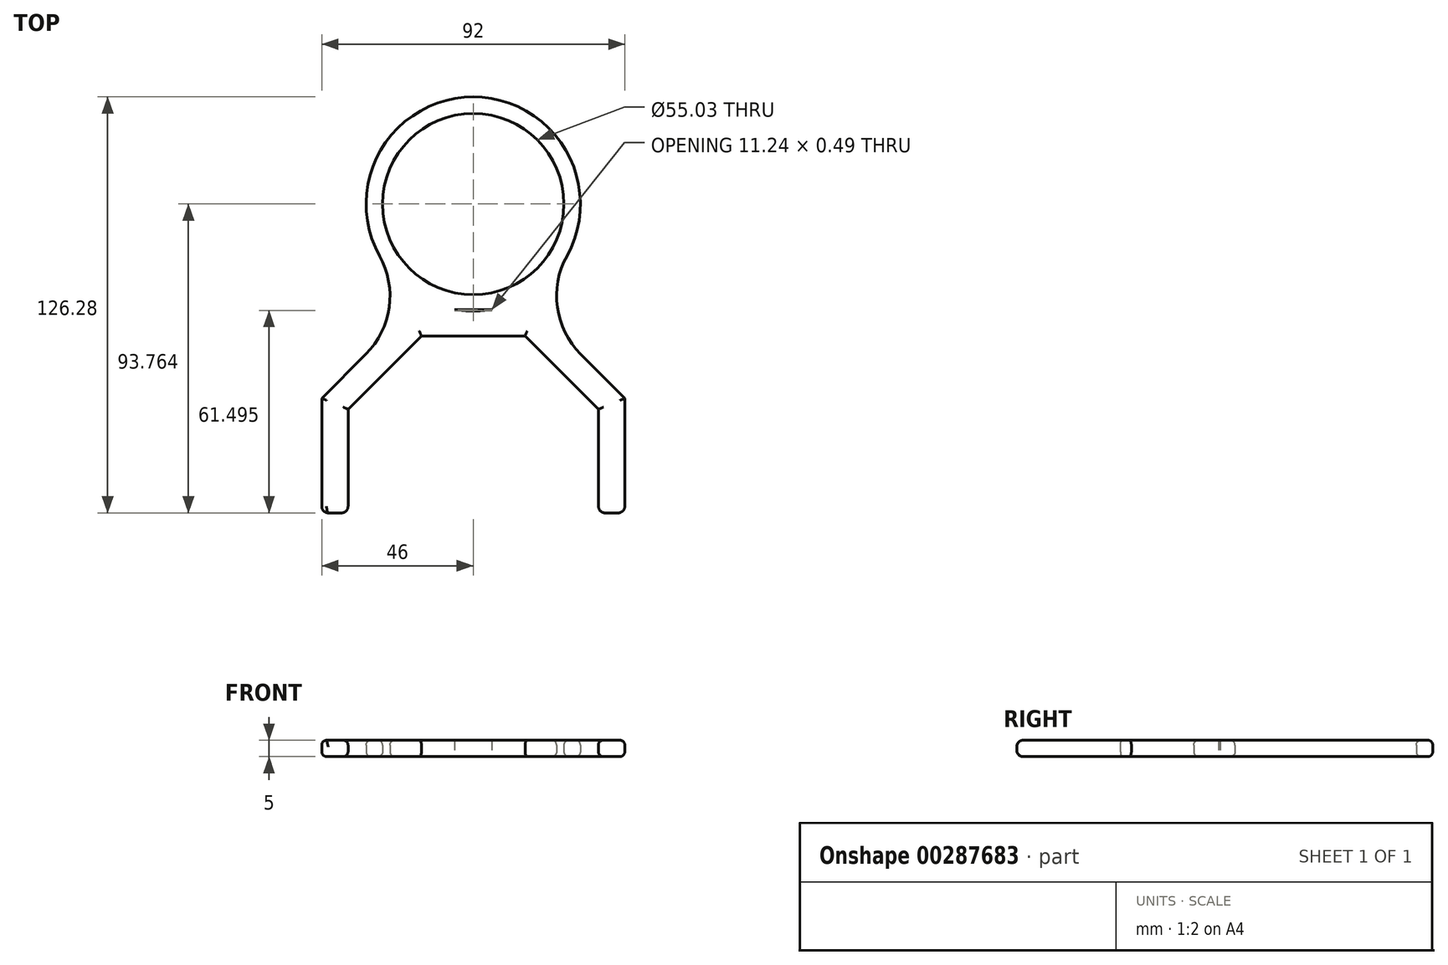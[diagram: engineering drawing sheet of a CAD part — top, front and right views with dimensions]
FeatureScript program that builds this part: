
annotation { "Feature Type Name" : "Feature", "Feature Type Description" : "" }
export const myFeature = defineFeature(function(context is Context, id is Id, definition is map)
    precondition{}
    {
        {
            var Q0;
            Q0=qCreatedBy(makeId("Top.planeOp"),FACE);
            var sketch = newSketch(context, id + "F0", { "sketchPlane" : qUnion([Q0])});
            skLineSegment(sketch, "E0.top", {"start": v(-46.8, 110.54) * mm, "end": v(46.8, 110.54) * mm});
            skLineSegment(sketch, "E0.left", {"start": v(-46.8, -31.71) * mm, "end": v(-46.8, 110.54) * mm});
            skLineSegment(sketch, "E0.right", {"start": v(46.8, -30.95) * mm, "end": v(46.8, 110.54) * mm});
            skCircle(sketch, "E1", {"center": v(0, 78.02) * mm, "radius": 32.51 * mm});
            skPoint(sketch, "E1.centerSnap0", {"position": v(0, 110.54) * mm});
            skLineSegment(sketch, "E2", {"start": v(-19.05, 46) * mm, "end": v(-28.16, 61.77) * mm});
            skLineSegment(sketch, "E3", {"start": v(28.16, 61.77) * mm, "end": v(19.05, 46) * mm});
            skCircle(sketch, "E4.0", {"center": v(0, 78.02) * mm, "radius": 27.51 * mm});
            skCircle(sketch, "E5.cCircle", {"center": v(0, 0) * mm, "radius": 38 * mm, "construction": true});
            skLineSegment(sketch, "E5.0", {"start": v(15.74, 38) * mm, "end": v(38, 15.74) * mm});
            skLineSegment(sketch, "E5.1", {"start": v(38, 15.74) * mm, "end": v(38, -15.74) * mm});
            skLineSegment(sketch, "E5.2", {"start": v(38, -15.74) * mm, "end": v(15.74, -38) * mm});
            skLineSegment(sketch, "E5.3", {"start": v(15.74, -38) * mm, "end": v(-15.74, -38) * mm});
            skLineSegment(sketch, "E5.4", {"start": v(-15.74, -38) * mm, "end": v(-38, -15.74) * mm});
            skLineSegment(sketch, "E5.5", {"start": v(-38, -15.74) * mm, "end": v(-38, 15.74) * mm});
            skLineSegment(sketch, "E5.6", {"start": v(-38, 15.74) * mm, "end": v(-15.74, 38) * mm});
            skLineSegment(sketch, "E5.7", {"start": v(-15.74, 38) * mm, "end": v(15.74, 38) * mm});
            skPoint(sketch, "E5.0.midPoint", {"position": v(26.87, 26.87) * mm});
            skLineSegment(sketch, "E6.0", {"start": v(-19.05, 46) * mm, "end": v(19.05, 46) * mm});
            skLineSegment(sketch, "E6.1", {"start": v(-46, 19.05) * mm, "end": v(-19.05, 46) * mm});
            skLineSegment(sketch, "E6.2", {"start": v(19.05, 46) * mm, "end": v(46, 19.05) * mm});
            skLineSegment(sketch, "E6.3", {"start": v(-46, -19.05) * mm, "end": v(-46, 19.05) * mm});
            skLineSegment(sketch, "E6.4", {"start": v(46, 19.05) * mm, "end": v(46, -19.05) * mm});
            skLineSegment(sketch, "E6.5", {"start": v(46, -19.05) * mm, "end": v(19.05, -46) * mm});
            skLineSegment(sketch, "E6.6", {"start": v(19.05, -46) * mm, "end": v(-19.05, -46) * mm});
            skLineSegment(sketch, "E6.7", {"start": v(-19.05, -46) * mm, "end": v(-46, -19.05) * mm});
            skLineSegment(sketch, "E7", {"start": v(-46.8, -15.74) * mm, "end": v(46.8, -15.74) * mm});
            skSolve(sketch);
        }
        {
            var Q0;
            Q0=makeQuery(id+"F0.imprint","IMPRINT",FACE,{"disambiguationData":[TD([[makeQuery(id+"F0.imprint","IMPRINT",EDGE,{"derivedFrom":sQuery(id+"F0.wireOp",EDGE,"E4.0")}),-1.0]])]});
            var Q1;
            {var subQ0=sQuery(id+"F0.wireOp",EDGE,"E2");Q1=makeQuery(id+"F0.imprint","IMPRINT",FACE,{"disambiguationData":[TD([[makeQuery(id+"F0.imprint","IMPRINT",EDGE,{"derivedFrom":subQ0}),-1.0]])]});}
            var Q2;
            Q2=makeQuery(id+"F0.imprint","IMPRINT",FACE,{"disambiguationData":[TD([[makeQuery(id+"F0.imprint","IMPRINT",EDGE,{"derivedFrom":sQuery(id+"F0.wireOp",EDGE,"1d4a6ea0-dfed-4e67-ae61-2447e46420ab.0")}),1.0]])]});
            var Q3;
            Q3=makeQuery(id+"F0.imprint","IMPRINT",FACE,{"disambiguationData":[TD([[makeQuery(id+"F0.imprint","IMPRINT",EDGE,{"derivedFrom":sQuery(id+"F0.wireOp",EDGE,"E5.0")}),1.0]])]});
            var Q4;
            {var subQ0=sQuery(id+"F0.wireOp",EDGE,"E3");Q4=makeQuery(id+"F0.imprint","IMPRINT",FACE,{"disambiguationData":[TD([[makeQuery(id+"F0.imprint","IMPRINT",EDGE,{"derivedFrom":subQ0}),-1.0]])]});}
            var Q5;
            {var subQ0=sQuery(id+"F0.wireOp",EDGE,"E6.0");var subQ1=sQuery(id+"F0.wireOp",EDGE,"E1");var subQ2=makeQuery(id+"F0.imprint","INTERSECT",VERTEX,{"disambiguationData":[OD(0.0)],"derivedFrom":[subQ1,subQ0]});Q5=makeQuery(id+"F0.imprint","IMPRINT",FACE,{"disambiguationData":[TD([[makeQuery(id+"F0.imprint","IMPRINT",EDGE,{"disambiguationData":[TD([[subQ2,-1.0]])],"derivedFrom":subQ1}),1.0]])]});}
            extrude(context, id + "F1", {"entities" : qUnion([Q0, Q1, Q2, Q3, Q4, Q5]), "depth" : 5 * mm});
        }
        {
            var Q0;
            Q0=makeQuery(id+"F1.opExtrude","SWEPT_EDGE",EDGE,{"disambiguationData":[OSD([sQuery(id+"F0.wireOp",EDGE,"E3"),sQuery(id+"F0.wireOp",EDGE,"E6.0"),sQuery(id+"F0.wireOp",EDGE,"E6.2")])]});
            var Q1;
            Q1=makeQuery(id+"F1.opExtrude","SWEPT_EDGE",EDGE,{"disambiguationData":[OSD([sQuery(id+"F0.wireOp",EDGE,"E2"),sQuery(id+"F0.wireOp",EDGE,"E6.0"),sQuery(id+"F0.wireOp",EDGE,"E6.1")])]});
            fillet(context, id + "F2", {"entities" : qUnion([Q0, Q1]), "radius" : 25 * mm, "tangentPropagation" : true, "allowEdgeOverflow" : false});
        }
        {
            var Q0;
            Q0=makeQuery(id+"F1.opExtrude","CAP_EDGE",EDGE,{"disambiguationData":[OSD([sQuery(id+"F0.wireOp",EDGE,"E4.0")])],"isStart":false});
            var Q1;
            Q1=makeQuery(id+"F1.opExtrude","CAP_EDGE",EDGE,{"disambiguationData":[OSD([sQuery(id+"F0.wireOp",EDGE,"E2")])],"isStart":false});
            var Q2;
            {var subQ0=sQuery(id+"F0.wireOp",EDGE,"E2");var subQ1=sQuery(id+"F0.wireOp",EDGE,"d9d4c305-0230-4e48-996b-9e131303d5f2.3");Q2=makeQuery(id+"F2.opFillet","BLEND_EDGE",EDGE,{"blendedFrom":[makeQuery(id+"F1.opExtrude","SWEPT_EDGE",EDGE,{"disambiguationData":[OSD([subQ1,subQ0])]}),makeQuery(id+"F1.opExtrude","CAP_FACE",FACE,{"disambiguationData":[OSD([sQuery(id+"F0.wireOp",EDGE,"1d4a6ea0-dfed-4e67-ae61-2447e46420ab.0"),sQuery(id+"F0.wireOp",EDGE,"1d4a6ea0-dfed-4e67-ae61-2447e46420ab.1"),sQuery(id+"F0.wireOp",EDGE,"1d4a6ea0-dfed-4e67-ae61-2447e46420ab.4"),sQuery(id+"F0.wireOp",EDGE,"1d4a6ea0-dfed-4e67-ae61-2447e46420ab.5"),sQuery(id+"F0.wireOp",EDGE,"d9d4c305-0230-4e48-996b-9e131303d5f2.1"),subQ1,sQuery(id+"F0.wireOp",EDGE,"E0.bottom"),sQuery(id+"F0.wireOp",EDGE,"E0.left"),sQuery(id+"F0.wireOp",EDGE,"E0.right"),sQuery(id+"F0.wireOp",EDGE,"E1"),subQ0,sQuery(id+"F0.wireOp",EDGE,"E3"),sQuery(id+"F0.wireOp",EDGE,"E4.0")])],"isStart":true})],"blendedInto":[makeQuery(id+"F1.opExtrude","CAP_FACE",FACE,{"disambiguationData":[OSD([sQuery(id+"F0.wireOp",EDGE,"1d4a6ea0-dfed-4e67-ae61-2447e46420ab.0"),sQuery(id+"F0.wireOp",EDGE,"1d4a6ea0-dfed-4e67-ae61-2447e46420ab.1"),sQuery(id+"F0.wireOp",EDGE,"1d4a6ea0-dfed-4e67-ae61-2447e46420ab.4"),sQuery(id+"F0.wireOp",EDGE,"1d4a6ea0-dfed-4e67-ae61-2447e46420ab.5"),sQuery(id+"F0.wireOp",EDGE,"d9d4c305-0230-4e48-996b-9e131303d5f2.1"),subQ1,sQuery(id+"F0.wireOp",EDGE,"E0.bottom"),sQuery(id+"F0.wireOp",EDGE,"E0.left"),sQuery(id+"F0.wireOp",EDGE,"E0.right"),sQuery(id+"F0.wireOp",EDGE,"E1"),subQ0,sQuery(id+"F0.wireOp",EDGE,"E3"),sQuery(id+"F0.wireOp",EDGE,"E4.0")])],"isStart":true})]});}
            var Q3;
            Q3=makeQuery(id+"F1.opExtrude","CAP_EDGE",EDGE,{"disambiguationData":[OSD([sQuery(id+"F0.wireOp",EDGE,"E4.0")])],"isStart":true});
            var Q4;
            Q4=makeQuery(id+"F1.opExtrude","CAP_EDGE",EDGE,{"disambiguationData":[OSD([sQuery(id+"F0.wireOp",EDGE,"1d4a6ea0-dfed-4e67-ae61-2447e46420ab.5")])],"isStart":false});
            var Q5;
            Q5=makeQuery(id+"F1.opExtrude","CAP_EDGE",EDGE,{"disambiguationData":[OSD([sQuery(id+"F0.wireOp",EDGE,"1d4a6ea0-dfed-4e67-ae61-2447e46420ab.0")])],"isStart":false});
            var Q6;
            Q6=makeQuery(id+"F1.opExtrude","CAP_EDGE",EDGE,{"disambiguationData":[OSD([sQuery(id+"F0.wireOp",EDGE,"1d4a6ea0-dfed-4e67-ae61-2447e46420ab.1")])],"isStart":false});
            var Q7;
            Q7=makeQuery(id+"F1.opExtrude","CAP_EDGE",EDGE,{"disambiguationData":[OSD([sQuery(id+"F0.wireOp",EDGE,"E0.right")])],"isStart":false});
            var Q8;
            Q8=makeQuery(id+"F1.opExtrude","CAP_EDGE",EDGE,{"disambiguationData":[OSD([sQuery(id+"F0.wireOp",EDGE,"1d4a6ea0-dfed-4e67-ae61-2447e46420ab.4")])],"isStart":false});
            var Q9;
            Q9=makeQuery(id+"F1.opExtrude","CAP_EDGE",EDGE,{"disambiguationData":[OSD([sQuery(id+"F0.wireOp",EDGE,"E0.left")])],"isStart":false});
            var Q10;
            Q10=makeQuery(id+"F1.opExtrude","CAP_EDGE",EDGE,{"disambiguationData":[OSD([sQuery(id+"F0.wireOp",EDGE,"E0.left")])],"isStart":true});
            var Q11;
            Q11=makeQuery(id+"F1.opExtrude","CAP_EDGE",EDGE,{"disambiguationData":[OSD([sQuery(id+"F0.wireOp",EDGE,"1d4a6ea0-dfed-4e67-ae61-2447e46420ab.5")])],"isStart":true});
            var Q12;
            Q12=makeQuery(id+"F1.opExtrude","CAP_EDGE",EDGE,{"disambiguationData":[OSD([sQuery(id+"F0.wireOp",EDGE,"1d4a6ea0-dfed-4e67-ae61-2447e46420ab.4")])],"isStart":true});
            var Q13;
            Q13=makeQuery(id+"F1.opExtrude","CAP_EDGE",EDGE,{"disambiguationData":[OSD([sQuery(id+"F0.wireOp",EDGE,"1d4a6ea0-dfed-4e67-ae61-2447e46420ab.1")])],"isStart":true});
            var Q14;
            Q14=makeQuery(id+"F1.opExtrude","CAP_EDGE",EDGE,{"disambiguationData":[OSD([sQuery(id+"F0.wireOp",EDGE,"E0.right")])],"isStart":true});
            var Q15;
            Q15=makeQuery(id+"F1.opExtrude","CAP_EDGE",EDGE,{"disambiguationData":[OSD([sQuery(id+"F0.wireOp",EDGE,"1d4a6ea0-dfed-4e67-ae61-2447e46420ab.0")])],"isStart":true});
            var Q16;
            Q16=makeQuery(id+"F1.opExtrude","CAP_EDGE",EDGE,{"disambiguationData":[OSD([sQuery(id+"F0.wireOp",EDGE,"E5.0")])],"isStart":true});
            var Q17;
            Q17=makeQuery(id+"F1.opExtrude","CAP_EDGE",EDGE,{"disambiguationData":[OSD([sQuery(id+"F0.wireOp",EDGE,"E5.7")])],"isStart":true});
            var Q18;
            Q18=makeQuery(id+"F1.opExtrude","CAP_EDGE",EDGE,{"disambiguationData":[OSD([sQuery(id+"F0.wireOp",EDGE,"E5.6")])],"isStart":true});
            var Q19;
            Q19=makeQuery(id+"F1.opExtrude","CAP_EDGE",EDGE,{"disambiguationData":[OSD([sQuery(id+"F0.wireOp",EDGE,"E5.5")])],"isStart":true});
            var Q20;
            Q20=makeQuery(id+"F1.opExtrude","CAP_EDGE",EDGE,{"disambiguationData":[OSD([sQuery(id+"F0.wireOp",EDGE,"E6.1")])],"isStart":true});
            var Q21;
            Q21=makeQuery(id+"F1.opExtrude","CAP_EDGE",EDGE,{"disambiguationData":[OSD([sQuery(id+"F0.wireOp",EDGE,"E6.3")])],"isStart":true});
            var Q22;
            Q22=makeQuery(id+"F1.opExtrude","CAP_EDGE",EDGE,{"disambiguationData":[OSD([sQuery(id+"F0.wireOp",EDGE,"E6.4")])],"isStart":true});
            var Q23;
            Q23=makeQuery(id+"F1.opExtrude","CAP_EDGE",EDGE,{"disambiguationData":[OSD([sQuery(id+"F0.wireOp",EDGE,"E5.1")])],"isStart":true});
            var Q24;
            {var subQ0=sQuery(id+"F0.wireOp",EDGE,"E6.1");var subQ1=sQuery(id+"F0.wireOp",EDGE,"E2");Q24=makeQuery(id+"F2.opFillet","BLEND_EDGE",EDGE,{"blendedFrom":[makeQuery(id+"F1.opExtrude","SWEPT_EDGE",EDGE,{"disambiguationData":[OSD([subQ1,sQuery(id+"F0.wireOp",EDGE,"E6.0"),subQ0])]}),makeQuery(id+"F1.opExtrude","CAP_FACE",FACE,{"disambiguationData":[OSD([sQuery(id+"F0.wireOp",EDGE,"E1"),subQ1,sQuery(id+"F0.wireOp",EDGE,"E3"),sQuery(id+"F0.wireOp",EDGE,"E4.0"),sQuery(id+"F0.wireOp",EDGE,"E5.0"),sQuery(id+"F0.wireOp",EDGE,"E5.1"),sQuery(id+"F0.wireOp",EDGE,"E5.5"),sQuery(id+"F0.wireOp",EDGE,"E5.6"),sQuery(id+"F0.wireOp",EDGE,"E5.7"),subQ0,sQuery(id+"F0.wireOp",EDGE,"E6.2"),sQuery(id+"F0.wireOp",EDGE,"E6.3"),sQuery(id+"F0.wireOp",EDGE,"E6.4"),sQuery(id+"F0.wireOp",EDGE,"E7")])],"isStart":false})],"blendedInto":[makeQuery(id+"F1.opExtrude","CAP_FACE",FACE,{"disambiguationData":[OSD([sQuery(id+"F0.wireOp",EDGE,"E1"),subQ1,sQuery(id+"F0.wireOp",EDGE,"E3"),sQuery(id+"F0.wireOp",EDGE,"E4.0"),sQuery(id+"F0.wireOp",EDGE,"E5.0"),sQuery(id+"F0.wireOp",EDGE,"E5.1"),sQuery(id+"F0.wireOp",EDGE,"E5.5"),sQuery(id+"F0.wireOp",EDGE,"E5.6"),sQuery(id+"F0.wireOp",EDGE,"E5.7"),subQ0,sQuery(id+"F0.wireOp",EDGE,"E6.2"),sQuery(id+"F0.wireOp",EDGE,"E6.3"),sQuery(id+"F0.wireOp",EDGE,"E6.4"),sQuery(id+"F0.wireOp",EDGE,"E7")])],"isStart":false})]});}
            var Q25;
            Q25=makeQuery(id+"F1.opExtrude","CAP_EDGE",EDGE,{"disambiguationData":[OSD([sQuery(id+"F0.wireOp",EDGE,"E6.3")])],"isStart":false});
            var Q26;
            Q26=makeQuery(id+"F1.opExtrude","CAP_EDGE",EDGE,{"disambiguationData":[OSD([sQuery(id+"F0.wireOp",EDGE,"E6.4")])],"isStart":false});
            var Q27;
            Q27=makeQuery(id+"F1.opExtrude","CAP_EDGE",EDGE,{"disambiguationData":[OSD([sQuery(id+"F0.wireOp",EDGE,"E5.0")])],"isStart":false});
            var Q28;
            Q28=makeQuery(id+"F1.opExtrude","CAP_EDGE",EDGE,{"disambiguationData":[OSD([sQuery(id+"F0.wireOp",EDGE,"E5.1")])],"isStart":false});
            var Q29;
            Q29=makeQuery(id+"F1.opExtrude","CAP_EDGE",EDGE,{"disambiguationData":[OSD([sQuery(id+"F0.wireOp",EDGE,"E5.7")])],"isStart":false});
            var Q30;
            Q30=makeQuery(id+"F1.opExtrude","CAP_EDGE",EDGE,{"disambiguationData":[OSD([sQuery(id+"F0.wireOp",EDGE,"E5.6")])],"isStart":false});
            var Q31;
            Q31=makeQuery(id+"F1.opExtrude","CAP_EDGE",EDGE,{"disambiguationData":[OSD([sQuery(id+"F0.wireOp",EDGE,"E5.5")])],"isStart":false});
            fillet(context, id + "F3", {"entities" : qUnion([Q0, Q1, Q2, Q3, Q4, Q5, Q6, Q7, Q8, Q9, Q10, Q11, Q12, Q13, Q14, Q15, Q16, Q17, Q18, Q19, Q20, Q21, Q22, Q23, Q24, Q25, Q26, Q27, Q28, Q29, Q30, Q31]), "radius" : 1.5 * mm, "tangentPropagation" : true, "allowEdgeOverflow" : false});
        }
        {
            var Q0;
            {var subQ0=sQuery(id+"F0.wireOp",EDGE,"E7");Q0=makeQuery(id+"F1.opExtrude","CAP_EDGE",EDGE,{"disambiguationData":[OSD([subQ0]),TDD([makeQuery(id+"F0.imprint","IMPRINT",EDGE,{"disambiguationData":[TD([[makeQuery(id+"F0.imprint","INTERSECT",VERTEX,{"derivedFrom":[sQuery(id+"F0.wireOp",EDGE,"E6.4"),subQ0]}),1.0]])],"derivedFrom":subQ0})])],"isStart":true});}
            var Q1;
            {var subQ0=sQuery(id+"F0.wireOp",EDGE,"E7");Q1=makeQuery(id+"F1.opExtrude","CAP_EDGE",EDGE,{"disambiguationData":[OSD([subQ0]),TDD([makeQuery(id+"F0.imprint","IMPRINT",EDGE,{"disambiguationData":[TD([[makeQuery(id+"F0.imprint","INTERSECT",VERTEX,{"derivedFrom":[sQuery(id+"F0.wireOp",EDGE,"E6.3"),subQ0]}),-1.0]])],"derivedFrom":subQ0})])],"isStart":true});}
            fillet(context, id + "F4", {"entities" : qUnion([Q0, Q1]), "radius" : 2 * mm, "tangentPropagation" : true, "allowEdgeOverflow" : false});
        }
    });
